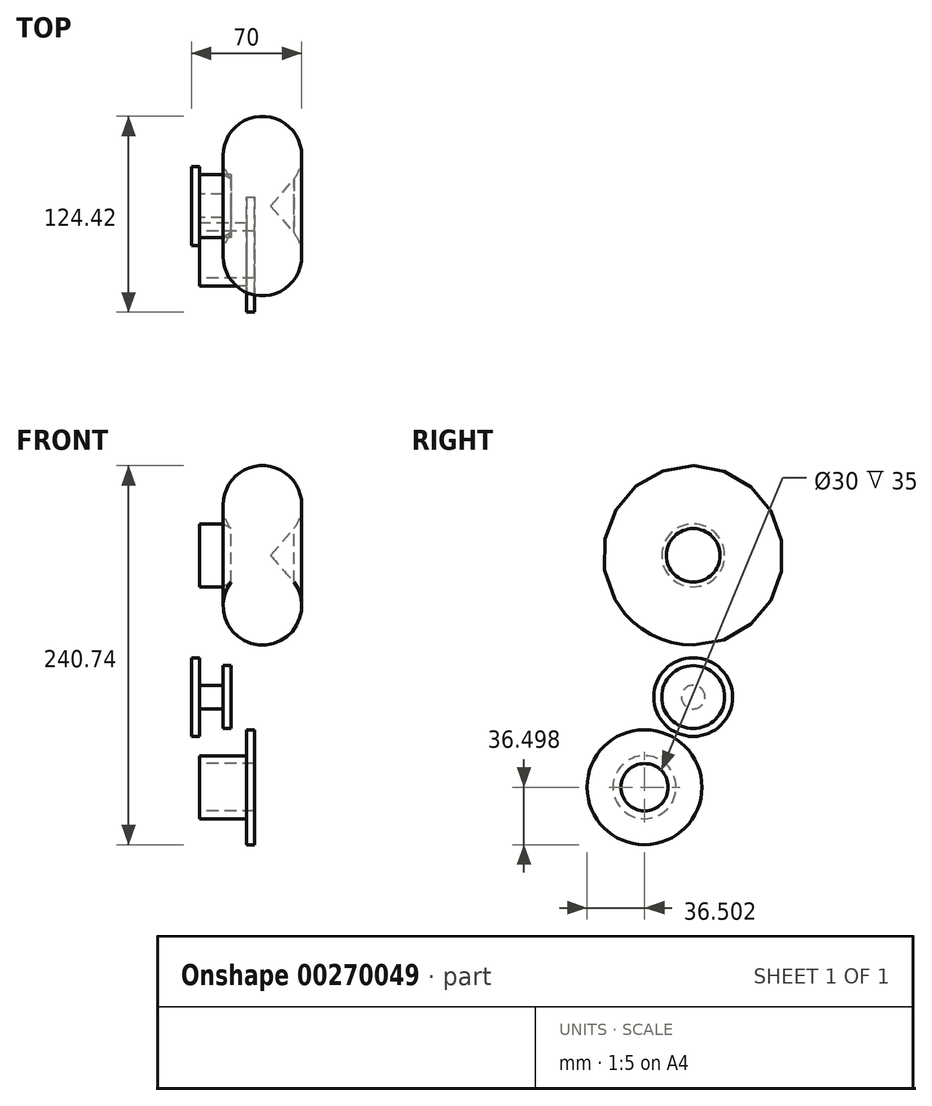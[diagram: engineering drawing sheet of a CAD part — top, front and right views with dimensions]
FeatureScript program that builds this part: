
annotation { "Feature Type Name" : "Feature", "Feature Type Description" : "" }
export const myFeature = defineFeature(function(context is Context, id is Id, definition is map)
    precondition{}
    {
        {
            var Q0;
            Q0=qCreatedBy(makeId("Right.planeOp"),FACE);
            var sketch = newSketch(context, id + "F0", { "sketchPlane" : qUnion([Q0])});
            skCircle(sketch, "E0", {"center": v(0, 0) * mm, "radius": 7.5 * mm});
            skSolve(sketch);
        }
        {
            var Q0;
            Q0=makeQuery(id+"F0.imprint","IMPRINT",FACE,{"disambiguationData":[TD([[makeQuery(id+"F0.imprint","IMPRINT",EDGE,{"derivedFrom":sQuery(id+"F0.wireOp",EDGE,"E0")}),1.0]])]});
            extrude(context, id + "F1", {"entities" : qUnion([Q0]), "depth" : 15 * mm});
        }
        {
            var Q0;
            Q0=makeQuery(id+"F1.opExtrude","CAP_FACE",FACE,{"disambiguationData":[OSD([sQuery(id+"F0.wireOp",EDGE,"E0")])],"isStart":false});
            var sketch = newSketch(context, id + "F2", { "sketchPlane" : qUnion([Q0])});
            skCircle(sketch, "E1", {"center": v(0, 0) * mm, "radius": 20 * mm});
            skSolve(sketch);
        }
        {
            var Q0;
            Q0=makeQuery(id+"F2.imprint","IMPRINT",FACE,{"disambiguationData":[TD([[makeQuery(id+"F2.imprint","IMPRINT",EDGE,{"derivedFrom":sQuery(id+"F2.wireOp",EDGE,"E1")}),1.0]])]});
            var Q1;
            Q1=makeQuery(id+"F2.imprint","IMPRINT",FACE,{"disambiguationData":[TD([[makeQuery(id+"F2.imprint","IMPRINT",EDGE,{"derivedFrom":makeQuery(id+"F1.opExtrude","CAP_EDGE",EDGE,{"disambiguationData":[OSD([sQuery(id+"F0.wireOp",EDGE,"E0")])],"isStart":false})}),1.0]])]});
            extrude(context, id + "F3", {"entities" : qUnion([Q0, Q1]), "operationType" : NewBodyOperationType.ADD, "depth" : 5 * mm});
        }
        {
            var Q0;
            Q0=qCreatedBy(makeId("Right.planeOp"),FACE);
            var sketch = newSketch(context, id + "F4", { "sketchPlane" : qUnion([Q0])});
            skCircle(sketch, "E2", {"center": v(-30.92, -57.24) * mm, "radius": 15 * mm});
            skCircle(sketch, "E3", {"center": v(-30.92, -57.24) * mm, "radius": 20 * mm});
            skSolve(sketch);
        }
        {
            var Q0;
            Q0=makeQuery(id+"F4.imprint","IMPRINT",FACE,{"disambiguationData":[TD([[makeQuery(id+"F4.imprint","IMPRINT",EDGE,{"derivedFrom":sQuery(id+"F4.wireOp",EDGE,"E2")}),-1.0]])]});
            extrude(context, id + "F5", {"entities" : qUnion([Q0]), "depth" : 35 * mm});
        }
        {
            var Q0;
            Q0=makeQuery(id+"F5.opExtrude","CAP_FACE",FACE,{"disambiguationData":[OSD([sQuery(id+"F4.wireOp",EDGE,"E2"),sQuery(id+"F4.wireOp",EDGE,"E3")])],"isStart":false});
            var sketch = newSketch(context, id + "F6", { "sketchPlane" : qUnion([Q0])});
            skCircle(sketch, "E4", {"center": v(-30.92, -57.24) * mm, "radius": 36.5 * mm});
            skCircle(sketch, "E5", {"center": v(-30.92, -57.24) * mm, "radius": 15 * mm});
            skSolve(sketch);
        }
        {
            var Q0;
            Q0=makeQuery(id+"F6.imprint","IMPRINT",FACE,{"disambiguationData":[TD([[makeQuery(id+"F6.imprint","IMPRINT",EDGE,{"derivedFrom":sQuery(id+"F6.wireOp",EDGE,"E4")}),1.0]])]});
            extrude(context, id + "F7", {"entities" : qUnion([Q0]), "operationType" : NewBodyOperationType.ADD, "oppositeDirection" : true, "depth" : 5 * mm});
        }
        {
            var Q0;
            Q0=makeQuery(id+"F1.opExtrude","CAP_FACE",FACE,{"disambiguationData":[OSD([sQuery(id+"F0.wireOp",EDGE,"E0")])],"isStart":true});
            var sketch = newSketch(context, id + "F8", { "sketchPlane" : qUnion([Q0])});
            skCircle(sketch, "E6", {"center": v(0, 0) * mm, "radius": 25 * mm});
            skSolve(sketch);
        }
        {
            var Q0;
            Q0=makeQuery(id+"F8.imprint","IMPRINT",FACE,{"disambiguationData":[TD([[makeQuery(id+"F8.imprint","IMPRINT",EDGE,{"derivedFrom":sQuery(id+"F8.wireOp",EDGE,"E6")}),1.0]])]});
            var Q1;
            Q1=makeQuery(id+"F8.imprint","IMPRINT",FACE,{"disambiguationData":[TD([[makeQuery(id+"F8.imprint","IMPRINT",EDGE,{"derivedFrom":makeQuery(id+"F1.opExtrude","CAP_EDGE",EDGE,{"disambiguationData":[OSD([sQuery(id+"F0.wireOp",EDGE,"E0")])],"isStart":true})}),-1.0]])]});
            extrude(context, id + "F9", {"entities" : qUnion([Q0, Q1]), "operationType" : NewBodyOperationType.ADD, "depth" : 5 * mm});
        }
        {
            var Q0;
            Q0=qCreatedBy(makeId("Right.planeOp"),FACE);
            var sketch = newSketch(context, id + "F10", { "sketchPlane" : qUnion([Q0])});
            skCircle(sketch, "E7", {"center": v(0, 90) * mm, "radius": 20 * mm});
            skSolve(sketch);
        }
        {
            var Q0;
            Q0=makeQuery(id+"F10.imprint","IMPRINT",FACE,{"disambiguationData":[TD([[makeQuery(id+"F10.imprint","IMPRINT",EDGE,{"derivedFrom":sQuery(id+"F10.wireOp",EDGE,"E7")}),1.0]])]});
            extrude(context, id + "F11", {"entities" : qUnion([Q0]), "depth" : 15 * mm});
        }
        {
            var Q0;
            Q0=qCreatedBy(makeId("Front.planeOp"),FACE);
            var sketch = newSketch(context, id + "F12", { "sketchPlane" : qUnion([Q0])});
            skLineSegment(sketch, "E8", {"start": v(15, 70) * mm, "end": v(20, 73) * mm});
            skArc(sketch, "E9", {"start": v(20, 73) * mm, "mid": v(40, 33) * mm, "end": v(60, 73) * mm});
            skLineSegment(sketch, "E10", {"start": v(60, 73) * mm, "end": v(45.2, 90) * mm});
            skLineSegment(sketch, "E11", {"start": v(45.2, 90) * mm, "end": v(15, 90) * mm});
            skLineSegment(sketch, "E12", {"start": v(15, 90) * mm, "end": v(15, 70) * mm});
            skSolve(sketch);
        }
        {
            var Q0;
            Q0=makeQuery(id+"F12.imprint","IMPRINT",FACE,{"disambiguationData":[TD([[makeQuery(id+"F12.imprint","IMPRINT",EDGE,{"derivedFrom":sQuery(id+"F12.wireOp",EDGE,"E8")}),1.0]])]});
            var Q1;
            Q1=sQuery(id+"F12.wireOp",EDGE,"E11");
            revolve(context, id + "F13", {"operationType" : NewBodyOperationType.ADD, "entities" : qUnion([Q0]), "axis" : qUnion([Q1]), "revolveType" : RevolveType.FULL});
        }
    });
